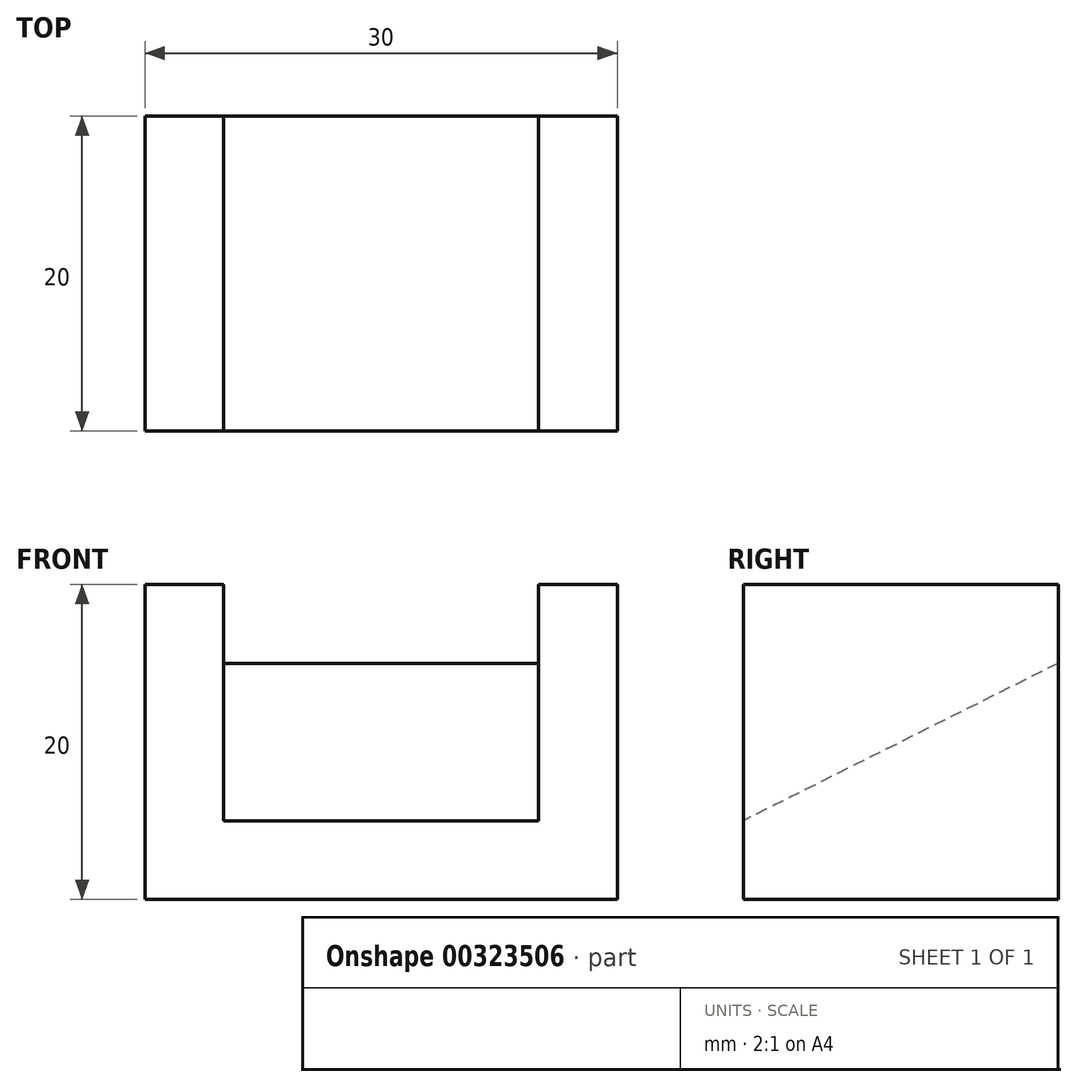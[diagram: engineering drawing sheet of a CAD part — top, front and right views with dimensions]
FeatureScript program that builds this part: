
annotation { "Feature Type Name" : "Feature", "Feature Type Description" : "" }
export const myFeature = defineFeature(function(context is Context, id is Id, definition is map)
    precondition{}
    {
        {
            var Q0;
            Q0=qCreatedBy(makeId("Right.planeOp"),FACE);
            var sketch = newSketch(context, id + "F0", { "sketchPlane" : qUnion([Q0])});
            skLineSegment(sketch, "E0.bottom", {"start": v(-10, 20) * mm, "end": v(10, 20) * mm});
            skLineSegment(sketch, "E0.top", {"start": v(-10, 0) * mm, "end": v(10, 0) * mm});
            skLineSegment(sketch, "E0.left", {"start": v(-10, 20) * mm, "end": v(-10, 0) * mm});
            skLineSegment(sketch, "E0.right", {"start": v(10, 20) * mm, "end": v(10, 0) * mm});
            skSolve(sketch);
        }
        {
            var Q0;
            Q0 = qSketchRegion(id + "F0", true);
            extrude(context, id + "F1", {"entities" : qUnion([Q0]), "endBound" : BoundingType.SYMMETRIC, "depth" : 30 * mm});
        }
        {
            var Q0;
            Q0=qCreatedBy(makeId("Right.planeOp"),FACE);
            var sketch = newSketch(context, id + "F2", { "sketchPlane" : qUnion([Q0])});
            skLineSegment(sketch, "E1.0.0", {"start": v(-10, 20) * mm, "end": v(-10, 5) * mm});
            skLineSegment(sketch, "E1.0.2", {"start": v(10, 15) * mm, "end": v(10, 20) * mm});
            skLineSegment(sketch, "E1.0.3", {"start": v(10, 20) * mm, "end": v(-10, 20) * mm});
            skLineSegment(sketch, "E2", {"start": v(10, 20) * mm, "end": v(10, 15) * mm});
            skLineSegment(sketch, "E3", {"start": v(10, 15) * mm, "end": v(-10, 5) * mm});
            skLineSegment(sketch, "E4", {"start": v(-10, 5) * mm, "end": v(-10, 20) * mm});
            skPoint(sketch, "E1.0.1.start.orphan", {"position": v(-10, 0) * mm});
            skPoint(sketch, "E5.orphan", {"position": v(10, 0) * mm});
            skSolve(sketch);
        }
        {
            var Q0;
            Q0 = qSketchRegion(id + "F2", true);
            extrude(context, id + "F3", {"entities" : qUnion([Q0]), "operationType" : NewBodyOperationType.REMOVE, "endBound" : BoundingType.SYMMETRIC, "oppositeDirection" : true, "depth" : 20 * mm});
        }
    });
